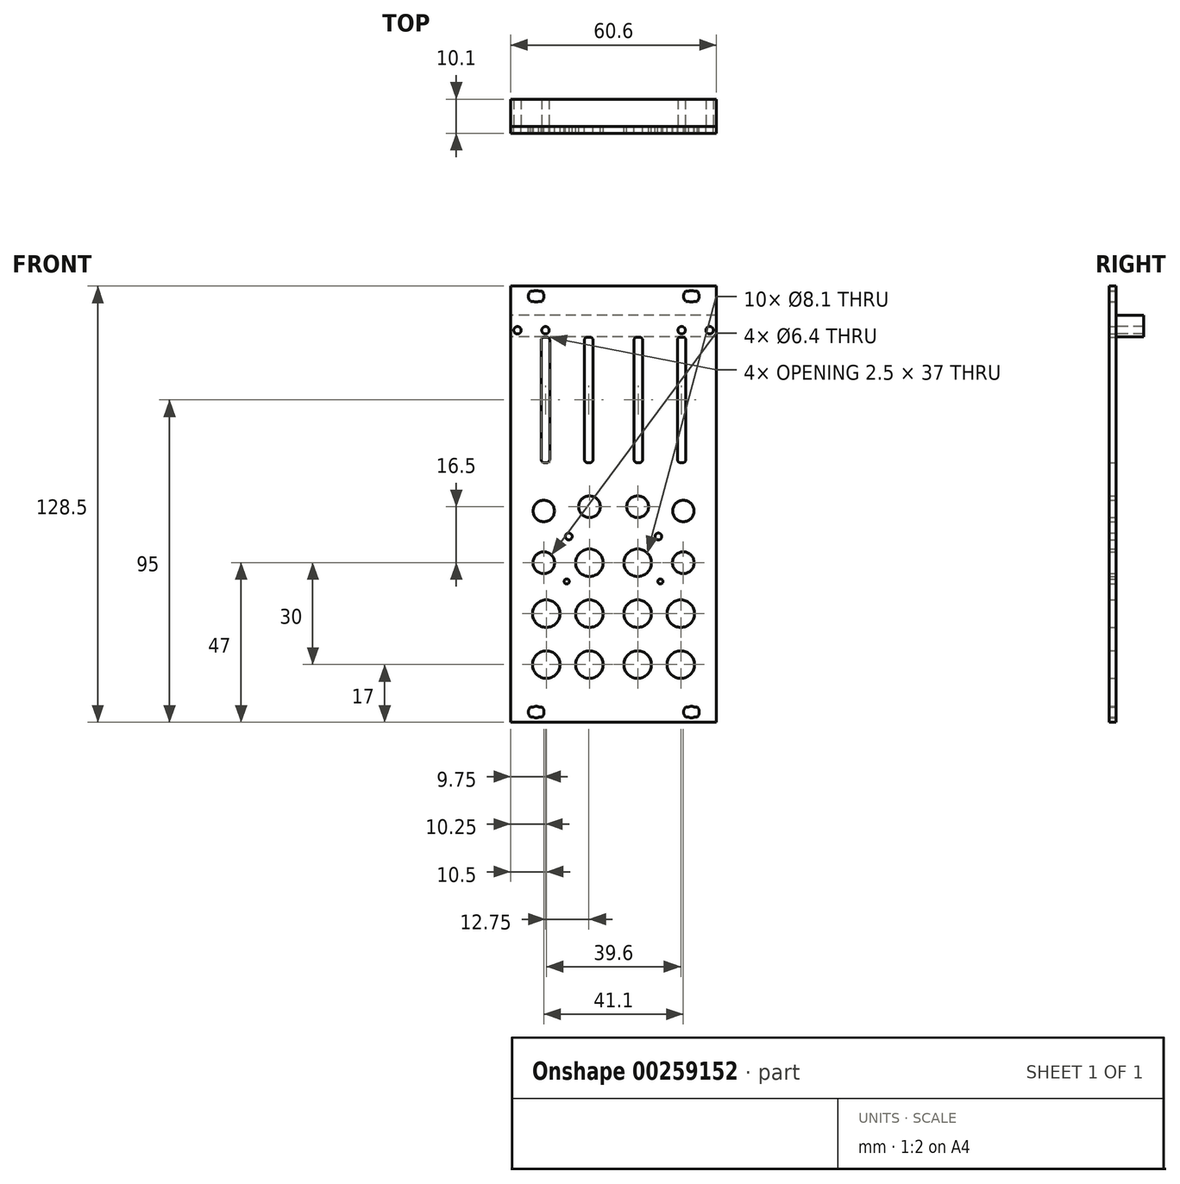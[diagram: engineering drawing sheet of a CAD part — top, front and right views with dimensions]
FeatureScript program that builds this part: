
annotation { "Feature Type Name" : "Feature", "Feature Type Description" : "" }
export const myFeature = defineFeature(function(context is Context, id is Id, definition is map)
    precondition{}
    {
        {
            var Q0;
            Q0=qCreatedBy(makeId("Front.planeOp"),FACE);
            var sketch = newSketch(context, id + "F0", { "sketchPlane" : qUnion([Q0])});
            skLineSegment(sketch, "E0", {"start": v(23.72, -59.75) * mm, "end": v(24.62, -59.75) * mm});
            skLineSegment(sketch, "E1", {"start": v(21.22, -59.75) * mm, "end": v(22.12, -59.75) * mm});
            skLineSegment(sketch, "E2", {"start": v(23.72, -62.75) * mm, "end": v(24.62, -62.75) * mm});
            skLineSegment(sketch, "E3", {"start": v(21.22, -62.75) * mm, "end": v(22.12, -62.75) * mm});
            skLineSegment(sketch, "E4", {"start": v(21.22, 59.75) * mm, "end": v(22.12, 59.75) * mm});
            skLineSegment(sketch, "E5", {"start": v(23.72, 59.75) * mm, "end": v(24.62, 59.75) * mm});
            skLineSegment(sketch, "E6", {"start": v(21.22, 62.75) * mm, "end": v(22.12, 62.75) * mm});
            skLineSegment(sketch, "E7", {"start": v(23.72, 62.75) * mm, "end": v(24.62, 62.75) * mm});
            skLineSegment(sketch, "E8", {"start": v(-30.3, -64.25) * mm, "end": v(-30.3, -61.25) * mm});
            skLineSegment(sketch, "E9", {"start": v(-30.3, 64.25) * mm, "end": v(30.3, 64.25) * mm});
            skLineSegment(sketch, "E10", {"start": v(30.3, -64.25) * mm, "end": v(30.3, 64.25) * mm});
            skLineSegment(sketch, "E11", {"start": v(-30.3, -64.25) * mm, "end": v(30.3, -64.25) * mm});
            skLineSegment(sketch, "E12", {"start": v(-30.3, -64.25) * mm, "end": v(-30.3, 64.25) * mm});
            skLineSegment(sketch, "E13", {"start": v(-22, -59.75) * mm, "end": v(-21.1, -59.75) * mm});
            skLineSegment(sketch, "E14", {"start": v(-24.5, -59.75) * mm, "end": v(-23.6, -59.75) * mm});
            skLineSegment(sketch, "E15", {"start": v(-22, -62.75) * mm, "end": v(-21.1, -62.75) * mm});
            skLineSegment(sketch, "E16", {"start": v(-24.5, -62.75) * mm, "end": v(-23.6, -62.75) * mm});
            skLineSegment(sketch, "E17", {"start": v(-22, 62.75) * mm, "end": v(-21.1, 62.75) * mm});
            skLineSegment(sketch, "E18", {"start": v(-24.5, 62.75) * mm, "end": v(-23.6, 62.75) * mm});
            skLineSegment(sketch, "E19", {"start": v(-22, 59.75) * mm, "end": v(-21.1, 59.75) * mm});
            skLineSegment(sketch, "E20", {"start": v(-24.5, 59.75) * mm, "end": v(-23.6, 59.75) * mm});
            skArc(sketch, "E21", {"start": v(21.22, -59.75) * mm, "mid": v(20.62, -61.25) * mm, "end": v(21.22, -62.75) * mm});
            skArc(sketch, "E22", {"start": v(24.62, -62.75) * mm, "mid": v(25.22, -61.25) * mm, "end": v(24.62, -59.75) * mm});
            skArc(sketch, "E23", {"start": v(23.72, -59.75) * mm, "mid": v(22.92, -59.55) * mm, "end": v(22.12, -59.75) * mm});
            skArc(sketch, "E24", {"start": v(22.12, -62.75) * mm, "mid": v(22.92, -62.95) * mm, "end": v(23.72, -62.75) * mm});
            skArc(sketch, "E25", {"start": v(22.12, 59.75) * mm, "mid": v(22.92, 59.55) * mm, "end": v(23.72, 59.75) * mm});
            skArc(sketch, "E26", {"start": v(23.72, 62.75) * mm, "mid": v(22.92, 62.95) * mm, "end": v(22.12, 62.75) * mm});
            skArc(sketch, "E27", {"start": v(24.62, 59.75) * mm, "mid": v(25.22, 61.25) * mm, "end": v(24.62, 62.75) * mm});
            skArc(sketch, "E28", {"start": v(21.22, 62.75) * mm, "mid": v(20.62, 61.25) * mm, "end": v(21.22, 59.75) * mm});
            skArc(sketch, "E29", {"start": v(-24.5, -59.75) * mm, "mid": v(-25.1, -61.25) * mm, "end": v(-24.5, -62.75) * mm});
            skArc(sketch, "E30", {"start": v(-21.1, -62.75) * mm, "mid": v(-20.5, -61.25) * mm, "end": v(-21.1, -59.75) * mm});
            skArc(sketch, "E31", {"start": v(-22, -59.75) * mm, "mid": v(-22.8, -59.55) * mm, "end": v(-23.6, -59.75) * mm});
            skArc(sketch, "E32", {"start": v(-23.6, -62.75) * mm, "mid": v(-22.8, -62.95) * mm, "end": v(-22, -62.75) * mm});
            skArc(sketch, "E33", {"start": v(-24.5, 62.75) * mm, "mid": v(-25.1, 61.25) * mm, "end": v(-24.5, 59.75) * mm});
            skArc(sketch, "E34", {"start": v(-21.1, 59.75) * mm, "mid": v(-20.5, 61.25) * mm, "end": v(-21.1, 62.75) * mm});
            skArc(sketch, "E35", {"start": v(-22, 62.75) * mm, "mid": v(-22.8, 62.95) * mm, "end": v(-23.6, 62.75) * mm});
            skArc(sketch, "E36", {"start": v(-23.6, 59.75) * mm, "mid": v(-22.8, 59.55) * mm, "end": v(-22, 59.75) * mm});
            skLineSegment(sketch, "E37", {"start": v(13.3, -22.75) * mm, "end": v(14.3, -22.75) * mm});
            skLineSegment(sketch, "E38", {"start": v(13.8, -23.25) * mm, "end": v(13.8, -22.25) * mm});
            skLineSegment(sketch, "E39", {"start": v(-20.55, -2.5) * mm, "end": v(-20.55, -1.5) * mm});
            skLineSegment(sketch, "E40", {"start": v(-21.05, -2) * mm, "end": v(-20.05, -2) * mm});
            skCircle(sketch, "E41", {"center": v(-20.55, -2) * mm, "radius": 3.15 * mm});
            skLineSegment(sketch, "E42", {"start": v(20.55, -2.5) * mm, "end": v(20.55, -1.5) * mm});
            skLineSegment(sketch, "E43", {"start": v(20.05, -2) * mm, "end": v(21.05, -2) * mm});
            skCircle(sketch, "E44", {"center": v(20.55, -2) * mm, "radius": 3.15 * mm});
            skLineSegment(sketch, "E45", {"start": v(6.05, 30.75) * mm, "end": v(6.05, 48.35) * mm});
            skLineSegment(sketch, "E46", {"start": v(6.05, 13.15) * mm, "end": v(6.05, 30.75) * mm});
            skLineSegment(sketch, "E47", {"start": v(6.95, 12.25) * mm, "end": v(7.65, 12.25) * mm});
            skLineSegment(sketch, "E48", {"start": v(7.3, 30.25) * mm, "end": v(7.3, 31.25) * mm});
            skLineSegment(sketch, "E49", {"start": v(8.55, 13.15) * mm, "end": v(8.55, 30.75) * mm});
            skLineSegment(sketch, "E50", {"start": v(6.8, 30.75) * mm, "end": v(7.8, 30.75) * mm});
            skLineSegment(sketch, "E51", {"start": v(6.95, 49.25) * mm, "end": v(7.65, 49.25) * mm});
            skLineSegment(sketch, "E52", {"start": v(8.55, 30.75) * mm, "end": v(8.55, 48.35) * mm});
            skArc(sketch, "E53", {"start": v(6.05, 13.15) * mm, "mid": v(6.31, 12.51) * mm, "end": v(6.95, 12.25) * mm});
            skArc(sketch, "E54", {"start": v(6.95, 49.25) * mm, "mid": v(6.31, 48.99) * mm, "end": v(6.05, 48.35) * mm});
            skArc(sketch, "E55", {"start": v(7.65, 12.25) * mm, "mid": v(8.29, 12.51) * mm, "end": v(8.55, 13.15) * mm});
            skArc(sketch, "E56", {"start": v(8.55, 48.35) * mm, "mid": v(8.29, 48.99) * mm, "end": v(7.65, 49.25) * mm});
            skLineSegment(sketch, "E57", {"start": v(-8.55, 30.75) * mm, "end": v(-8.55, 48.35) * mm});
            skLineSegment(sketch, "E58", {"start": v(-8.55, 13.15) * mm, "end": v(-8.55, 30.75) * mm});
            skLineSegment(sketch, "E59", {"start": v(-7.65, 12.25) * mm, "end": v(-6.95, 12.25) * mm});
            skLineSegment(sketch, "E60", {"start": v(-7.3, 30.25) * mm, "end": v(-7.3, 31.25) * mm});
            skLineSegment(sketch, "E61", {"start": v(-6.05, 13.15) * mm, "end": v(-6.05, 30.75) * mm});
            skLineSegment(sketch, "E62", {"start": v(-7.8, 30.75) * mm, "end": v(-6.8, 30.75) * mm});
            skLineSegment(sketch, "E63", {"start": v(-7.65, 49.25) * mm, "end": v(-6.95, 49.25) * mm});
            skLineSegment(sketch, "E64", {"start": v(-6.05, 30.75) * mm, "end": v(-6.05, 48.35) * mm});
            skArc(sketch, "E65", {"start": v(-8.55, 13.15) * mm, "mid": v(-8.29, 12.51) * mm, "end": v(-7.65, 12.25) * mm});
            skArc(sketch, "E66", {"start": v(-7.65, 49.25) * mm, "mid": v(-8.29, 48.99) * mm, "end": v(-8.55, 48.35) * mm});
            skArc(sketch, "E67", {"start": v(-6.95, 12.25) * mm, "mid": v(-6.31, 12.51) * mm, "end": v(-6.05, 13.15) * mm});
            skArc(sketch, "E68", {"start": v(-6.05, 48.35) * mm, "mid": v(-6.31, 48.99) * mm, "end": v(-6.95, 49.25) * mm});
            skLineSegment(sketch, "E69", {"start": v(18.8, 30.75) * mm, "end": v(18.8, 48.35) * mm});
            skLineSegment(sketch, "E70", {"start": v(18.8, 13.15) * mm, "end": v(18.8, 30.75) * mm});
            skLineSegment(sketch, "E71", {"start": v(19.7, 12.25) * mm, "end": v(20.4, 12.25) * mm});
            skLineSegment(sketch, "E72", {"start": v(20.05, 30.25) * mm, "end": v(20.05, 31.25) * mm});
            skLineSegment(sketch, "E73", {"start": v(21.3, 13.15) * mm, "end": v(21.3, 30.75) * mm});
            skLineSegment(sketch, "E74", {"start": v(19.55, 30.75) * mm, "end": v(20.55, 30.75) * mm});
            skLineSegment(sketch, "E75", {"start": v(19.7, 49.25) * mm, "end": v(20.4, 49.25) * mm});
            skLineSegment(sketch, "E76", {"start": v(21.3, 30.75) * mm, "end": v(21.3, 48.35) * mm});
            skArc(sketch, "E77", {"start": v(18.8, 13.15) * mm, "mid": v(19.06, 12.51) * mm, "end": v(19.7, 12.25) * mm});
            skArc(sketch, "E78", {"start": v(19.7, 49.25) * mm, "mid": v(19.06, 48.99) * mm, "end": v(18.8, 48.35) * mm});
            skArc(sketch, "E79", {"start": v(20.4, 12.25) * mm, "mid": v(21.04, 12.51) * mm, "end": v(21.3, 13.15) * mm});
            skArc(sketch, "E80", {"start": v(21.3, 48.35) * mm, "mid": v(21.04, 48.99) * mm, "end": v(20.4, 49.25) * mm});
            skLineSegment(sketch, "E81", {"start": v(-21.3, 30.75) * mm, "end": v(-21.3, 48.35) * mm});
            skLineSegment(sketch, "E82", {"start": v(-21.3, 13.15) * mm, "end": v(-21.3, 30.75) * mm});
            skLineSegment(sketch, "E83", {"start": v(-20.4, 12.25) * mm, "end": v(-19.7, 12.25) * mm});
            skLineSegment(sketch, "E84", {"start": v(-20.05, 30.25) * mm, "end": v(-20.05, 31.25) * mm});
            skLineSegment(sketch, "E85", {"start": v(-18.8, 13.15) * mm, "end": v(-18.8, 30.75) * mm});
            skLineSegment(sketch, "E86", {"start": v(-20.55, 30.75) * mm, "end": v(-19.55, 30.75) * mm});
            skLineSegment(sketch, "E87", {"start": v(-20.4, 49.25) * mm, "end": v(-19.7, 49.25) * mm});
            skLineSegment(sketch, "E88", {"start": v(-18.8, 30.75) * mm, "end": v(-18.8, 48.35) * mm});
            skArc(sketch, "E89", {"start": v(-21.3, 13.15) * mm, "mid": v(-21.04, 12.51) * mm, "end": v(-20.4, 12.25) * mm});
            skArc(sketch, "E90", {"start": v(-20.4, 49.25) * mm, "mid": v(-21.04, 48.99) * mm, "end": v(-21.3, 48.35) * mm});
            skArc(sketch, "E91", {"start": v(-19.7, 12.25) * mm, "mid": v(-19.06, 12.51) * mm, "end": v(-18.8, 13.15) * mm});
            skArc(sketch, "E92", {"start": v(-18.8, 48.35) * mm, "mid": v(-19.06, 48.99) * mm, "end": v(-19.7, 49.25) * mm});
            skCircle(sketch, "E93", {"center": v(-20.05, 51.25) * mm, "radius": 1.1 * mm});
            skLineSegment(sketch, "E94", {"start": v(-14.3, -22.75) * mm, "end": v(-13.3, -22.75) * mm});
            skLineSegment(sketch, "E95", {"start": v(-13.8, -23.25) * mm, "end": v(-13.8, -22.25) * mm});
            skLineSegment(sketch, "E96", {"start": v(13.2, -10) * mm, "end": v(13.2, -9) * mm});
            skLineSegment(sketch, "E97", {"start": v(12.7, -9.5) * mm, "end": v(13.7, -9.5) * mm});
            skLineSegment(sketch, "E98", {"start": v(-13.2, -10) * mm, "end": v(-13.2, -9) * mm});
            skLineSegment(sketch, "E99", {"start": v(-13.7, -9.5) * mm, "end": v(-12.7, -9.5) * mm});
            skLineSegment(sketch, "E100", {"start": v(7.1, -1.25) * mm, "end": v(7.1, -0.25) * mm});
            skLineSegment(sketch, "E101", {"start": v(6.6, -0.75) * mm, "end": v(7.6, -0.75) * mm});
            skCircle(sketch, "E102", {"center": v(7.1, -0.75) * mm, "radius": 3.2 * mm});
            skLineSegment(sketch, "E103", {"start": v(-7.1, -1.25) * mm, "end": v(-7.1, -0.25) * mm});
            skLineSegment(sketch, "E104", {"start": v(-7.6, -0.75) * mm, "end": v(-6.6, -0.75) * mm});
            skCircle(sketch, "E105", {"center": v(-7.1, -0.75) * mm, "radius": 3.2 * mm});
            skLineSegment(sketch, "E106", {"start": v(20.55, -17.75) * mm, "end": v(20.55, -16.75) * mm});
            skLineSegment(sketch, "E107", {"start": v(20.05, -17.25) * mm, "end": v(21.05, -17.25) * mm});
            skCircle(sketch, "E108", {"center": v(20.55, -17.25) * mm, "radius": 3.2 * mm});
            skLineSegment(sketch, "E109", {"start": v(-20.55, -17.75) * mm, "end": v(-20.55, -16.75) * mm});
            skLineSegment(sketch, "E110", {"start": v(-21.05, -17.25) * mm, "end": v(-20.05, -17.25) * mm});
            skCircle(sketch, "E111", {"center": v(-20.55, -17.25) * mm, "radius": 3.2 * mm});
            skLineSegment(sketch, "E112", {"start": v(6.35, -17.25) * mm, "end": v(7.85, -17.25) * mm});
            skLineSegment(sketch, "E113", {"start": v(7.1, -18) * mm, "end": v(7.1, -16.5) * mm});
            skCircle(sketch, "E114", {"center": v(7.1, -17.25) * mm, "radius": 4.05 * mm});
            skLineSegment(sketch, "E115", {"start": v(19.05, -32.25) * mm, "end": v(20.55, -32.25) * mm});
            skLineSegment(sketch, "E116", {"start": v(19.8, -33) * mm, "end": v(19.8, -31.5) * mm});
            skCircle(sketch, "E117", {"center": v(19.8, -32.25) * mm, "radius": 4.05 * mm});
            skLineSegment(sketch, "E118", {"start": v(6.35, -32.25) * mm, "end": v(7.85, -32.25) * mm});
            skLineSegment(sketch, "E119", {"start": v(7.1, -33) * mm, "end": v(7.1, -31.5) * mm});
            skCircle(sketch, "E120", {"center": v(7.1, -32.25) * mm, "radius": 4.05 * mm});
            skLineSegment(sketch, "E121", {"start": v(19.05, -47.25) * mm, "end": v(20.55, -47.25) * mm});
            skLineSegment(sketch, "E122", {"start": v(19.8, -48) * mm, "end": v(19.8, -46.5) * mm});
            skCircle(sketch, "E123", {"center": v(19.8, -47.25) * mm, "radius": 4.05 * mm});
            skLineSegment(sketch, "E124", {"start": v(6.35, -47.25) * mm, "end": v(7.85, -47.25) * mm});
            skLineSegment(sketch, "E125", {"start": v(7.1, -48) * mm, "end": v(7.1, -46.5) * mm});
            skCircle(sketch, "E126", {"center": v(7.1, -47.25) * mm, "radius": 4.05 * mm});
            skLineSegment(sketch, "E127", {"start": v(-7.85, -17.25) * mm, "end": v(-6.35, -17.25) * mm});
            skLineSegment(sketch, "E128", {"start": v(-7.1, -18) * mm, "end": v(-7.1, -16.5) * mm});
            skCircle(sketch, "E129", {"center": v(-7.1, -17.25) * mm, "radius": 4.05 * mm});
            skLineSegment(sketch, "E130", {"start": v(-20.55, -32.25) * mm, "end": v(-19.05, -32.25) * mm});
            skLineSegment(sketch, "E131", {"start": v(-19.8, -33) * mm, "end": v(-19.8, -31.5) * mm});
            skCircle(sketch, "E132", {"center": v(-19.8, -32.25) * mm, "radius": 4.05 * mm});
            skLineSegment(sketch, "E133", {"start": v(-7.85, -32.25) * mm, "end": v(-6.35, -32.25) * mm});
            skLineSegment(sketch, "E134", {"start": v(-7.1, -33) * mm, "end": v(-7.1, -31.5) * mm});
            skCircle(sketch, "E135", {"center": v(-7.1, -32.25) * mm, "radius": 4.05 * mm});
            skLineSegment(sketch, "E136", {"start": v(-20.55, -47.25) * mm, "end": v(-19.05, -47.25) * mm});
            skLineSegment(sketch, "E137", {"start": v(-19.8, -48) * mm, "end": v(-19.8, -46.5) * mm});
            skCircle(sketch, "E138", {"center": v(-19.8, -47.25) * mm, "radius": 4.05 * mm});
            skLineSegment(sketch, "E139", {"start": v(-7.85, -47.25) * mm, "end": v(-6.35, -47.25) * mm});
            skLineSegment(sketch, "E140", {"start": v(-7.1, -48) * mm, "end": v(-7.1, -46.5) * mm});
            skCircle(sketch, "E141", {"center": v(-7.1, -47.25) * mm, "radius": 4.05 * mm});
            skLineSegment(sketch, "E142", {"start": v(19.42, 51.25) * mm, "end": v(20.69, 51.25) * mm});
            skLineSegment(sketch, "E143", {"start": v(20.05, 50.62) * mm, "end": v(20.05, 51.89) * mm});
            skCircle(sketch, "E144", {"center": v(20.05, 51.25) * mm, "radius": 1.1 * mm});
            skLineSegment(sketch, "E145", {"start": v(-20.69, 51.25) * mm, "end": v(-19.41, 51.25) * mm});
            skLineSegment(sketch, "E146", {"start": v(-20.05, 50.62) * mm, "end": v(-20.05, 51.89) * mm});
            skCircle(sketch, "E147", {"center": v(-13.8, -22.75) * mm, "radius": 0.75 * mm});
            skCircle(sketch, "E148", {"center": v(-13.2, -9.5) * mm, "radius": 1 * mm});
            skCircle(sketch, "E149", {"center": v(13.2, -9.5) * mm, "radius": 1 * mm});
            skCircle(sketch, "E150", {"center": v(13.8, -22.75) * mm, "radius": 0.75 * mm});
            skSolve(sketch);
        }
        {
            var Q0;
            Q0=qSketchRegion(id+"F0",true);
            extrude(context, id + "F1", {"entities" : qUnion([Q0]), "depth" : 2 * mm, "offsetDistance" : 25 * mm});
        }
        {
            var Q0;
            Q0=makeQuery(id+"F1.opExtrude","CAP_FACE",FACE,{"disambiguationData":[OSD([sQuery(id+"F0.wireOp",EDGE,"E0"),sQuery(id+"F0.wireOp",EDGE,"E1"),sQuery(id+"F0.wireOp",EDGE,"E2"),sQuery(id+"F0.wireOp",EDGE,"E3"),sQuery(id+"F0.wireOp",EDGE,"E4"),sQuery(id+"F0.wireOp",EDGE,"E5"),sQuery(id+"F0.wireOp",EDGE,"E6"),sQuery(id+"F0.wireOp",EDGE,"E7"),sQuery(id+"F0.wireOp",EDGE,"E9"),sQuery(id+"F0.wireOp",EDGE,"E10"),sQuery(id+"F0.wireOp",EDGE,"E11"),sQuery(id+"F0.wireOp",EDGE,"E12"),sQuery(id+"F0.wireOp",EDGE,"E13"),sQuery(id+"F0.wireOp",EDGE,"E14"),sQuery(id+"F0.wireOp",EDGE,"E15"),sQuery(id+"F0.wireOp",EDGE,"E16"),sQuery(id+"F0.wireOp",EDGE,"E17"),sQuery(id+"F0.wireOp",EDGE,"E18"),sQuery(id+"F0.wireOp",EDGE,"E19"),sQuery(id+"F0.wireOp",EDGE,"E20"),sQuery(id+"F0.wireOp",EDGE,"E21"),sQuery(id+"F0.wireOp",EDGE,"E22"),sQuery(id+"F0.wireOp",EDGE,"E23"),sQuery(id+"F0.wireOp",EDGE,"E24"),sQuery(id+"F0.wireOp",EDGE,"E25"),sQuery(id+"F0.wireOp",EDGE,"E26"),sQuery(id+"F0.wireOp",EDGE,"E27"),sQuery(id+"F0.wireOp",EDGE,"E28"),sQuery(id+"F0.wireOp",EDGE,"E29"),sQuery(id+"F0.wireOp",EDGE,"E30"),sQuery(id+"F0.wireOp",EDGE,"E31"),sQuery(id+"F0.wireOp",EDGE,"E32"),sQuery(id+"F0.wireOp",EDGE,"E33"),sQuery(id+"F0.wireOp",EDGE,"E34"),sQuery(id+"F0.wireOp",EDGE,"E35"),sQuery(id+"F0.wireOp",EDGE,"E36"),sQuery(id+"F0.wireOp",EDGE,"E41"),sQuery(id+"F0.wireOp",EDGE,"E44"),sQuery(id+"F0.wireOp",EDGE,"E45"),sQuery(id+"F0.wireOp",EDGE,"E46"),sQuery(id+"F0.wireOp",EDGE,"E47"),sQuery(id+"F0.wireOp",EDGE,"E49"),sQuery(id+"F0.wireOp",EDGE,"E51"),sQuery(id+"F0.wireOp",EDGE,"E52"),sQuery(id+"F0.wireOp",EDGE,"E53"),sQuery(id+"F0.wireOp",EDGE,"E54"),sQuery(id+"F0.wireOp",EDGE,"E55"),sQuery(id+"F0.wireOp",EDGE,"E56"),sQuery(id+"F0.wireOp",EDGE,"E57"),sQuery(id+"F0.wireOp",EDGE,"E58"),sQuery(id+"F0.wireOp",EDGE,"E59"),sQuery(id+"F0.wireOp",EDGE,"E61"),sQuery(id+"F0.wireOp",EDGE,"E63"),sQuery(id+"F0.wireOp",EDGE,"E64"),sQuery(id+"F0.wireOp",EDGE,"E65"),sQuery(id+"F0.wireOp",EDGE,"E66"),sQuery(id+"F0.wireOp",EDGE,"E67"),sQuery(id+"F0.wireOp",EDGE,"E68"),sQuery(id+"F0.wireOp",EDGE,"E69"),sQuery(id+"F0.wireOp",EDGE,"E70"),sQuery(id+"F0.wireOp",EDGE,"E71"),sQuery(id+"F0.wireOp",EDGE,"E73"),sQuery(id+"F0.wireOp",EDGE,"E75"),sQuery(id+"F0.wireOp",EDGE,"E76"),sQuery(id+"F0.wireOp",EDGE,"E77"),sQuery(id+"F0.wireOp",EDGE,"E78"),sQuery(id+"F0.wireOp",EDGE,"E79"),sQuery(id+"F0.wireOp",EDGE,"E80"),sQuery(id+"F0.wireOp",EDGE,"E81"),sQuery(id+"F0.wireOp",EDGE,"E82"),sQuery(id+"F0.wireOp",EDGE,"E83"),sQuery(id+"F0.wireOp",EDGE,"E85"),sQuery(id+"F0.wireOp",EDGE,"E87"),sQuery(id+"F0.wireOp",EDGE,"E88"),sQuery(id+"F0.wireOp",EDGE,"E89"),sQuery(id+"F0.wireOp",EDGE,"E90"),sQuery(id+"F0.wireOp",EDGE,"E91"),sQuery(id+"F0.wireOp",EDGE,"E92"),sQuery(id+"F0.wireOp",EDGE,"E93"),sQuery(id+"F0.wireOp",EDGE,"E102"),sQuery(id+"F0.wireOp",EDGE,"E105"),sQuery(id+"F0.wireOp",EDGE,"E108"),sQuery(id+"F0.wireOp",EDGE,"E111"),sQuery(id+"F0.wireOp",EDGE,"E114"),sQuery(id+"F0.wireOp",EDGE,"E117"),sQuery(id+"F0.wireOp",EDGE,"E120"),sQuery(id+"F0.wireOp",EDGE,"E123"),sQuery(id+"F0.wireOp",EDGE,"E126"),sQuery(id+"F0.wireOp",EDGE,"E129"),sQuery(id+"F0.wireOp",EDGE,"E132"),sQuery(id+"F0.wireOp",EDGE,"E135"),sQuery(id+"F0.wireOp",EDGE,"E138"),sQuery(id+"F0.wireOp",EDGE,"E141"),sQuery(id+"F0.wireOp",EDGE,"E144"),sQuery(id+"F0.wireOp",EDGE,"E147"),sQuery(id+"F0.wireOp",EDGE,"E148"),sQuery(id+"F0.wireOp",EDGE,"E149"),sQuery(id+"F0.wireOp",EDGE,"E150")])],"isStart":true});
            var sketch = newSketch(context, id + "F2", { "sketchPlane" : qUnion([Q0])});
            skLineSegment(sketch, "E151", {"start": v(0, 64.25) * mm, "end": v(0, -64.25) * mm, "construction": true});
            skPoint(sketch, "E152", {"position": v(-20.05, 51.25) * mm});
            skLineSegment(sketch, "E153.MirrorCS", {"start": v(-40.1, 64.25) * mm, "end": v(-40.1, -64.25) * mm, "construction": true});
            skPoint(sketch, "E154.MirrorP", {"position": v(20.05, 51.25) * mm});
            skCircle(sketch, "E155.0", {"center": v(-20.05, 51.25) * mm, "radius": 1.1 * mm});
            skCircle(sketch, "E156.0", {"center": v(20.05, 51.25) * mm, "radius": 1.1 * mm});
            skLineSegment(sketch, "E157.bottom", {"start": v(-30.3, 55.71) * mm, "end": v(30.3, 55.71) * mm});
            skLineSegment(sketch, "E157.top", {"start": v(-30.3, 49.36) * mm, "end": v(30.3, 49.36) * mm});
            skLineSegment(sketch, "E157.left", {"start": v(-30.3, 55.71) * mm, "end": v(-30.3, 49.36) * mm});
            skLineSegment(sketch, "E157.right", {"start": v(30.3, 55.71) * mm, "end": v(30.3, 49.36) * mm});
            skLineSegment(sketch, "E158", {"start": v(0, 55.71) * mm, "end": v(0, 49.36) * mm, "construction": true});
            skPoint(sketch, "E159.centerSnap0", {"position": v(0, 52.54) * mm});
            skCircle(sketch, "E160", {"center": v(-28.3, 51.25) * mm, "radius": 1.1 * mm});
            skCircle(sketch, "E161.MirrorC", {"center": v(28.3, 51.25) * mm, "radius": 1.1 * mm});
            skSolve(sketch);
        }
        {
            var Q0;
            Q0=qSketchRegion(id+"F2",true);
            extrude(context, id + "F3", {"entities" : qUnion([Q0]), "depth" : 8.1 * mm, "offsetDistance" : 25 * mm});
        }
        {
            var Q0;
            Q0=makeQuery(id+"F1.opExtrude","CAP_FACE",FACE,{"disambiguationData":[OSD([sQuery(id+"F0.wireOp",EDGE,"E0"),sQuery(id+"F0.wireOp",EDGE,"E1"),sQuery(id+"F0.wireOp",EDGE,"E2"),sQuery(id+"F0.wireOp",EDGE,"E3"),sQuery(id+"F0.wireOp",EDGE,"E4"),sQuery(id+"F0.wireOp",EDGE,"E5"),sQuery(id+"F0.wireOp",EDGE,"E6"),sQuery(id+"F0.wireOp",EDGE,"E7"),sQuery(id+"F0.wireOp",EDGE,"E9"),sQuery(id+"F0.wireOp",EDGE,"E10"),sQuery(id+"F0.wireOp",EDGE,"E11"),sQuery(id+"F0.wireOp",EDGE,"E12"),sQuery(id+"F0.wireOp",EDGE,"E13"),sQuery(id+"F0.wireOp",EDGE,"E14"),sQuery(id+"F0.wireOp",EDGE,"E15"),sQuery(id+"F0.wireOp",EDGE,"E16"),sQuery(id+"F0.wireOp",EDGE,"E17"),sQuery(id+"F0.wireOp",EDGE,"E18"),sQuery(id+"F0.wireOp",EDGE,"E19"),sQuery(id+"F0.wireOp",EDGE,"E20"),sQuery(id+"F0.wireOp",EDGE,"E21"),sQuery(id+"F0.wireOp",EDGE,"E22"),sQuery(id+"F0.wireOp",EDGE,"E23"),sQuery(id+"F0.wireOp",EDGE,"E24"),sQuery(id+"F0.wireOp",EDGE,"E25"),sQuery(id+"F0.wireOp",EDGE,"E26"),sQuery(id+"F0.wireOp",EDGE,"E27"),sQuery(id+"F0.wireOp",EDGE,"E28"),sQuery(id+"F0.wireOp",EDGE,"E29"),sQuery(id+"F0.wireOp",EDGE,"E30"),sQuery(id+"F0.wireOp",EDGE,"E31"),sQuery(id+"F0.wireOp",EDGE,"E32"),sQuery(id+"F0.wireOp",EDGE,"E33"),sQuery(id+"F0.wireOp",EDGE,"E34"),sQuery(id+"F0.wireOp",EDGE,"E35"),sQuery(id+"F0.wireOp",EDGE,"E36"),sQuery(id+"F0.wireOp",EDGE,"E41"),sQuery(id+"F0.wireOp",EDGE,"E44"),sQuery(id+"F0.wireOp",EDGE,"E45"),sQuery(id+"F0.wireOp",EDGE,"E46"),sQuery(id+"F0.wireOp",EDGE,"E47"),sQuery(id+"F0.wireOp",EDGE,"E49"),sQuery(id+"F0.wireOp",EDGE,"E51"),sQuery(id+"F0.wireOp",EDGE,"E52"),sQuery(id+"F0.wireOp",EDGE,"E53"),sQuery(id+"F0.wireOp",EDGE,"E54"),sQuery(id+"F0.wireOp",EDGE,"E55"),sQuery(id+"F0.wireOp",EDGE,"E56"),sQuery(id+"F0.wireOp",EDGE,"E57"),sQuery(id+"F0.wireOp",EDGE,"E58"),sQuery(id+"F0.wireOp",EDGE,"E59"),sQuery(id+"F0.wireOp",EDGE,"E61"),sQuery(id+"F0.wireOp",EDGE,"E63"),sQuery(id+"F0.wireOp",EDGE,"E64"),sQuery(id+"F0.wireOp",EDGE,"E65"),sQuery(id+"F0.wireOp",EDGE,"E66"),sQuery(id+"F0.wireOp",EDGE,"E67"),sQuery(id+"F0.wireOp",EDGE,"E68"),sQuery(id+"F0.wireOp",EDGE,"E69"),sQuery(id+"F0.wireOp",EDGE,"E70"),sQuery(id+"F0.wireOp",EDGE,"E71"),sQuery(id+"F0.wireOp",EDGE,"E73"),sQuery(id+"F0.wireOp",EDGE,"E75"),sQuery(id+"F0.wireOp",EDGE,"E76"),sQuery(id+"F0.wireOp",EDGE,"E77"),sQuery(id+"F0.wireOp",EDGE,"E78"),sQuery(id+"F0.wireOp",EDGE,"E79"),sQuery(id+"F0.wireOp",EDGE,"E80"),sQuery(id+"F0.wireOp",EDGE,"E81"),sQuery(id+"F0.wireOp",EDGE,"E82"),sQuery(id+"F0.wireOp",EDGE,"E83"),sQuery(id+"F0.wireOp",EDGE,"E85"),sQuery(id+"F0.wireOp",EDGE,"E87"),sQuery(id+"F0.wireOp",EDGE,"E88"),sQuery(id+"F0.wireOp",EDGE,"E89"),sQuery(id+"F0.wireOp",EDGE,"E90"),sQuery(id+"F0.wireOp",EDGE,"E91"),sQuery(id+"F0.wireOp",EDGE,"E92"),sQuery(id+"F0.wireOp",EDGE,"E93"),sQuery(id+"F0.wireOp",EDGE,"E102"),sQuery(id+"F0.wireOp",EDGE,"E105"),sQuery(id+"F0.wireOp",EDGE,"E108"),sQuery(id+"F0.wireOp",EDGE,"E111"),sQuery(id+"F0.wireOp",EDGE,"E114"),sQuery(id+"F0.wireOp",EDGE,"E117"),sQuery(id+"F0.wireOp",EDGE,"E120"),sQuery(id+"F0.wireOp",EDGE,"E123"),sQuery(id+"F0.wireOp",EDGE,"E126"),sQuery(id+"F0.wireOp",EDGE,"E129"),sQuery(id+"F0.wireOp",EDGE,"E132"),sQuery(id+"F0.wireOp",EDGE,"E135"),sQuery(id+"F0.wireOp",EDGE,"E138"),sQuery(id+"F0.wireOp",EDGE,"E141"),sQuery(id+"F0.wireOp",EDGE,"E144"),sQuery(id+"F0.wireOp",EDGE,"E147"),sQuery(id+"F0.wireOp",EDGE,"E148"),sQuery(id+"F0.wireOp",EDGE,"E149"),sQuery(id+"F0.wireOp",EDGE,"E150")])],"isStart":true});
            var sketch = newSketch(context, id + "F4", { "sketchPlane" : qUnion([Q0])});
            skCircle(sketch, "E162.0", {"center": v(-28.3, 51.25) * mm, "radius": 1.1 * mm});
            skCircle(sketch, "E163.0", {"center": v(28.3, 51.25) * mm, "radius": 1.1 * mm});
            skSolve(sketch);
        }
        {
            var Q0;
            Q0 = qSketchRegion(id + "F4", true);
            extrude(context, id + "F5", {"entities" : qUnion([Q0]), "operationType" : NewBodyOperationType.REMOVE, "oppositeDirection" : true, "depth" : 25 * mm, "offsetDistance" : 25 * mm});
        }
    });
